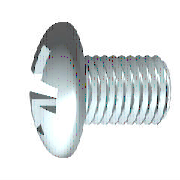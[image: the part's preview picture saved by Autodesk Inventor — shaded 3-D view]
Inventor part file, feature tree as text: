
AUTODESK INVENTOR PART (.ipt)
format: ipt  version: 2020 (Build 240168000, 168)  size: 291,840 bytes
history: native  units: mm (DEFAULTED — no unit token found)
features: other x2, plane x2, extrude x1
ambient origin geometry x7: Origin, YZ Plane, XZ Plane, X Axis, Y Axis, Z Axis, Center Point
bodies: Solid1 (feature_tree)
feature tree (5):
  other  "Базовый элемент"
  plane  "Work Plane1"
  extrude  "Паз"  Depth=6.0mm
  other  "Вырез"
  plane  "Work Plane3"
